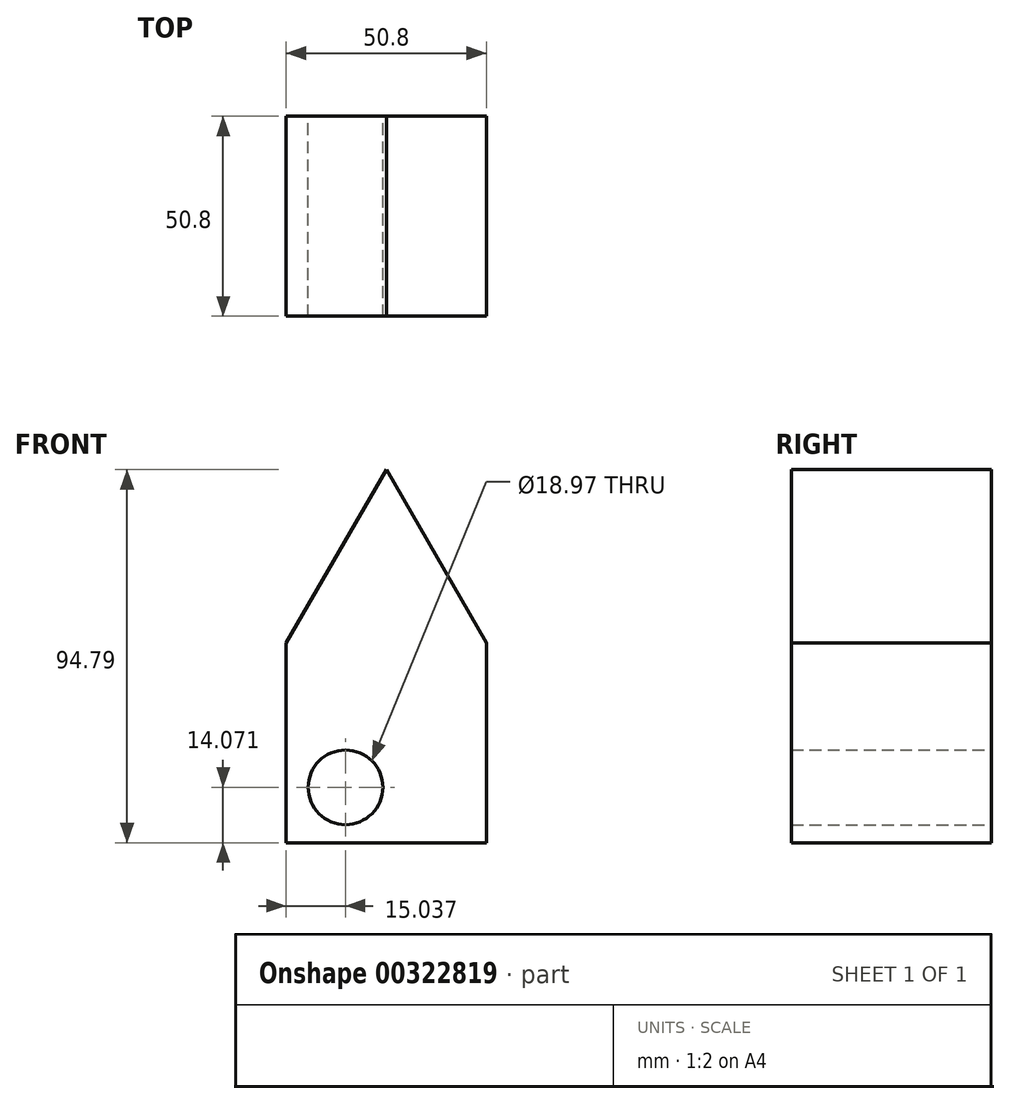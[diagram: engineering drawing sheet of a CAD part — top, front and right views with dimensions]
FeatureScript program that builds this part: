
annotation { "Feature Type Name" : "Feature", "Feature Type Description" : "" }
export const myFeature = defineFeature(function(context is Context, id is Id, definition is map)
    precondition{}
    {
        {
            var Q0;
            Q0=qCreatedBy(makeId("Front.planeOp"),FACE);
            var sketch = newSketch(context, id + "F0", { "sketchPlane" : qUnion([Q0])});
            skLineSegment(sketch, "E0.top", {"start": v(-25.4, -34.34) * mm, "end": v(25.4, -34.34) * mm});
            skLineSegment(sketch, "E0.left", {"start": v(-25.4, 16.46) * mm, "end": v(-25.4, -34.34) * mm});
            skLineSegment(sketch, "E0.right", {"start": v(25.4, 16.46) * mm, "end": v(25.4, -34.34) * mm});
            skLineSegment(sketch, "E1", {"start": v(-25.4, 16.46) * mm, "end": v(0, 60.45) * mm});
            skLineSegment(sketch, "E2", {"start": v(25.4, 16.46) * mm, "end": v(0, 60.45) * mm});
            skCircle(sketch, "E3", {"center": v(-10.36, -20.27) * mm, "radius": 9.48 * mm});
            skSolve(sketch);
        }
        {
            var Q0;
            Q0=makeQuery(id+"F0.imprint","IMPRINT",FACE,{"disambiguationData":[TD([[makeQuery(id+"F0.imprint","IMPRINT",EDGE,{"derivedFrom":sQuery(id+"F0.wireOp",EDGE,"E0.top")}),1.0]])]});
            extrude(context, id + "F1", {"entities" : qUnion([Q0]), "depth" : 50.8 * mm});
        }
    });
